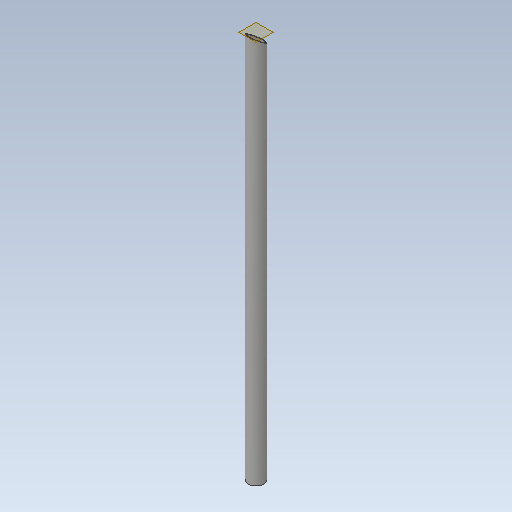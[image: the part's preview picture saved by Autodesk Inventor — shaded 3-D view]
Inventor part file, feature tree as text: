
AUTODESK INVENTOR PART (.ipt)
format: ipt  version: 2020.1 (Build 241239000, 239)  size: 91,648 bytes
history: native  units: mm
features: extrude x2, sketch x2, plane x1
ambient origin geometry x8: Origin, YZ Plane, XZ Plane, XY Plane, X Axis, Y Axis, Z Axis, Center Point
bodies: Solid1 (feature_tree)
feature tree (5):
  extrude  "Extrusion1"  Depth=3.75mm
  extrude  "skrå ende"  Depth=10.0mm TaperAngle=0.0deg
  plane  "Work Plane3"
  sketch  "Sketch1"  dims[d0=48.5mm d1=3.75mm]
  sketch  "Sketch2"  dims[d2=41.0mm d3=1200.0mm d4=0.0mm d5=5.986479mm d6=10.0mm d7=0.0mm]
